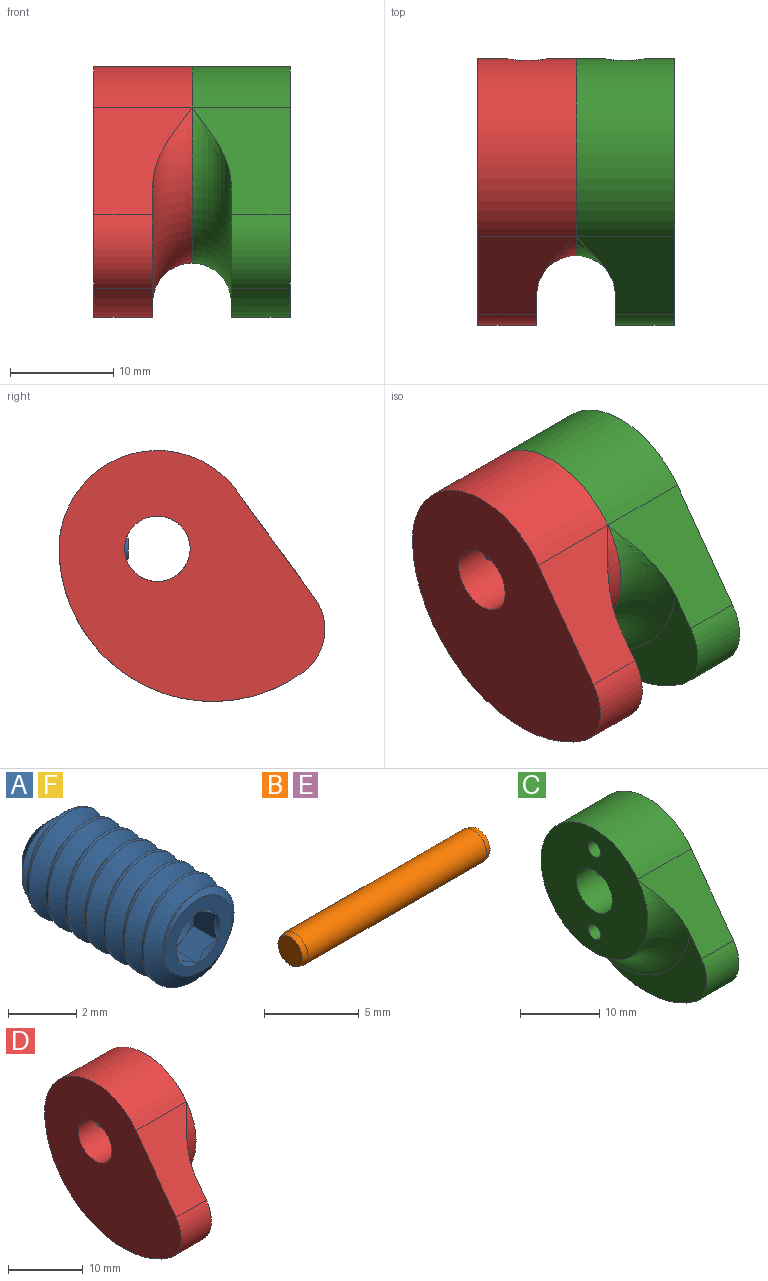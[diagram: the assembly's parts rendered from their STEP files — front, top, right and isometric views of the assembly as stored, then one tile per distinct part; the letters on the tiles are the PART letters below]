
ASSEMBLY  parts=6 mates=5
PART A: 27 faces, bbox 3.9x7x3.9 mm
  f0: cone r=0.79mm half-angle=60deg, axis (0,-1,0), area 2.3mm2, adj f1,f22,f23,f24,f25,f26
  f1: plane 0.69x0.4mm, normal (0,-1,0), area 0mm2, adj f0,f2,f21
  f2: plane 1.08x1.01mm, normal (-1,0,0), area 0.8mm2, adj f1,f3,f20,f21,f22
  f3: plane 1.34x1.14mm, normal (-0.5,0,-0.87), area 0.8mm2, adj f2,f4,f19,f22,f23
  f4: plane 1.34x1.14mm, normal (0.5,0,-0.87), area 0.8mm2, adj f3,f5,f18,f23,f24
  f5: plane 1.34x1.26mm, normal (1,0,0), area 0.8mm2, adj f4,f6,f17,f24,f25
  f6: plane 1.34x1.14mm, normal (0.5,0,0.87), area 0.8mm2, adj f5,f7,f21,f25,f26
  f7: cone r=0.92mm half-angle=45deg, axis (0,-1,0), area 0mm2, adj f6,f8
  f8: plane 2.84x2.7mm, normal (0,-1,0), area 3.2mm2, adj f7,f9,f10,f14,f15,f16,f17,f18
  f9: cone r=0.92mm half-angle=45deg, axis (0,-1,0), area 0mm2, adj f8,f21
  f10: cylinder r=1.24mm len=6.07mm, axis (0,-1,0), area 5.9mm2, adj f8,f11,f14,f16
  f11: cone r=0.96mm half-angle=45deg, axis (0,-1,0), area 6mm2, adj f10,f12,f13,f14,f16
  f12: cylinder r=1.75mm len=5.31mm, axis (0,-1,0), area 7.3mm2, adj f11,f14,f15,f16
  f13: cone r=1664.28mm half-angle=59deg, axis (0,1,0), area 3.4mm2, adj f11
  f14: bspline ~6.37x3.51mm, area 40.3mm2, adj f8,f10,f11,f12,f15
  f15: cone r=1.75mm half-angle=55deg, axis (0,1,0), area 1.6mm2, adj f8,f12,f14,f16
  f16: bspline ~6.47x3.5mm, area 40.3mm2, adj f8,f10,f11,f12,f15
  f17: cone r=0.92mm half-angle=45deg, axis (0,-1,0), area 0mm2, adj f5,f8
  f18: cone r=0.92mm half-angle=45deg, axis (0,-1,0), area 0mm2, adj f4,f8
  f19: cone r=0.92mm half-angle=45deg, axis (0,-1,0), area 0mm2, adj f3,f8
  f20: cone r=0.92mm half-angle=45deg, axis (0,-1,0), area 0.1mm2, adj f2,f8
  f21: plane 1.34x1.14mm, normal (-0.5,0,0.87), area 0.8mm2, adj f1,f2,f6,f9,f26
  f22: plane 0.69x0.4mm, normal (0,-1,0), area 0mm2, adj f0,f2,f3
  f23: plane 0.79x0.23mm, normal (0,-1,0), area 0mm2, adj f0,f3,f4
  f24: plane 0.69x0.4mm, normal (0,-1,0), area 0mm2, adj f0,f4,f5
  f25: plane 0.69x0.4mm, normal (0,-1,0), area 0mm2, adj f0,f5,f6
  f26: plane 0.79x0.23mm, normal (0,-1,0), area 0mm2, adj f0,f6,f21
PART B: 5 faces, bbox 14x2x2 mm
  f0: cone r=1mm half-angle=15deg, axis (1,0,0), area 2.2mm2, adj f2,f4
  f1: cone r=1mm half-angle=15deg, axis (-1,0,0), area 2.2mm2, adj f2,f3
  f2: cylinder r=1mm len=13.3mm, axis (1,0,0), area 83.6mm2, adj f0,f1
  f3: plane 1.81x1.81mm, normal (1,0,0), area 2.6mm2, adj f1
  f4: plane 1.81x1.81mm, normal (-1,0,0), area 2.6mm2, adj f0
PART C: 16 faces, bbox 13.3x35.8x28.7 mm
  f0: cylinder r=5.12mm len=7.16mm, axis (-1,0,0), area 46mm2, adj f1,f2,f4,f6
  f1: plane 17.41x12.84mm, normal (-1,0,0), area 70.1mm2, adj f0,f2,f4,f5
  f2: cylinder r=14.9mm len=23.65mm, axis (-1,0,0), area 211.6mm2, adj f0,f1,f3,f5,f6,f11
  f3: cylinder r=9.53mm len=17.23mm, axis (-1,0,0), area 223.1mm2, adj f2,f4,f6,f8,f10
  f4: plane 11.5x10.63mm, normal (0,-0.81,0.59), area 86.5mm2, adj f0,f1,f3,f5,f6
  f5: torus R=13.33mm, axis (1,0,0), area 167.4mm2, adj f1,f2,f4,f8
  f6: plane 25.76x24.32mm, normal (1,0,0), area 418.3mm2, adj f0,f2,f3,f4,f7
  f7: cylinder r=3.17mm len=9.53mm, axis (-1,0,0), area 184.9mm2, adj f6,f8,f9
  f8: plane 19.05x19.05mm, normal (-1,0,0), area 245.8mm2, adj f3,f5,f7,f12,f14
  f9: cylinder r=1.39mm len=6.17mm, axis (0,-1,0), area 51.5mm2, adj f7,f10,f11
  f10: bspline ~3.86x2.17mm, area 4.1mm2, adj f3,f9,f11
  f11: bspline ~3.76x1.83mm, area 3.6mm2, adj f2,f9,f10
  f12: cylinder r=1.1mm len=7.5mm, axis (1,0,0), area 51.8mm2, adj f8,f13
  f13: plane 2.2x2.2mm, normal (-1,0,0), area 3.8mm2, adj f12
  f14: cylinder r=1.1mm len=7.5mm, axis (1,0,0), area 51.8mm2, adj f8,f15
  f15: plane 2.2x2.2mm, normal (-1,0,0), area 3.8mm2, adj f14
PART D: 16 faces, bbox 10.6x35.8x28.7 mm
  f0: cylinder r=5.12mm len=7.16mm, axis (1,0,0), area 46mm2, adj f1,f2,f4,f6
  f1: plane 17.41x12.84mm, normal (1,0,0), area 70.1mm2, adj f0,f2,f4,f5
  f2: cylinder r=14.9mm len=23.65mm, axis (1,0,0), area 211.6mm2, adj f0,f1,f3,f5,f6,f11
  f3: cylinder r=9.53mm len=17.23mm, axis (1,0,0), area 223.1mm2, adj f2,f4,f6,f8,f10
  f4: plane 11.5x10.63mm, normal (0,-0.81,0.59), area 86.5mm2, adj f0,f1,f3,f5,f6
  f5: torus R=13.33mm, axis (-1,0,0), area 167.4mm2, adj f1,f2,f4,f8
  f6: plane 25.76x24.32mm, normal (-1,0,0), area 418.3mm2, adj f0,f2,f3,f4,f7
  f7: cylinder r=3.17mm len=9.53mm, axis (1,0,0), area 184.9mm2, adj f6,f8,f9
  f8: plane 19.05x19.05mm, normal (1,0,0), area 245.8mm2, adj f3,f5,f7,f12,f14
  f9: cylinder r=1.39mm len=6.17mm, axis (0,-1,0), area 51.5mm2, adj f7,f10,f11
  f10: bspline ~3.86x2.17mm, area 4.1mm2, adj f3,f9,f11
  f11: bspline ~3.76x1.83mm, area 3.6mm2, adj f2,f9,f10
  f12: cylinder r=1.1mm len=7.5mm, axis (-1,0,0), area 51.8mm2, adj f8,f13
  f13: plane 2.2x2.2mm, normal (1,0,0), area 3.8mm2, adj f12
  f14: cylinder r=1.1mm len=7.5mm, axis (-1,0,0), area 51.8mm2, adj f8,f15
  f15: plane 2.2x2.2mm, normal (1,0,0), area 3.8mm2, adj f14
PART E: same geometry as B
PART F: same geometry as A
PLACE A rot(axis=(-1,0,0),180deg) t=(-4.76,6.28,0)mm
PLACE B t=(0,0,-6.35)mm
PLACE C t=(0,0,-92.39)mm
PLACE D t=(0,0,-92.39)mm
PLACE E t=(0,0,6.35)mm
PLACE F rot(axis=(-1,0,0),180deg) t=(4.76,6.28,0)mm
MATE fastened F.f13 <-> C.f9  axis (0,1,0) through (4.76,2.81,0)mm
MATE fastened B.f0 <-> D.f12  axis (1,0,0) through (0,0,-6.35)mm
MATE fastened C.f3 <-> D.f3  axis (-1,0,0) through (0,0,0)mm
MATE fastened E.f0 <-> D.f14  axis (1,0,0) through (0,0,6.35)mm
MATE fastened A.f13 <-> D.f9  axis (0,1,0) through (-4.76,2.81,0)mm
